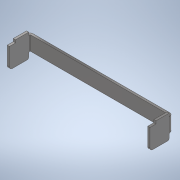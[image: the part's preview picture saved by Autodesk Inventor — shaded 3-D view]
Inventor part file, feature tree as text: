
AUTODESK INVENTOR PART (.ipt)
format: ipt  version: 2020 (Build 240168000, 168)  size: 299,520 bytes
history: native  units: mm
features: other x4, extrude x1
ambient origin geometry x8: Origin, YZ Plane, XZ Plane, XY Plane, X Axis, Y Axis, Z Axis, Center Point
bodies: Body1 (feature_tree)
feature tree (5):
  other  "實體1"
  extrude  "擠出1"  Depth=2.0mm TaperAngle=0.0deg
  other  "折彎零件1"
  other  "折彎零件2"
  other  "定義1"
